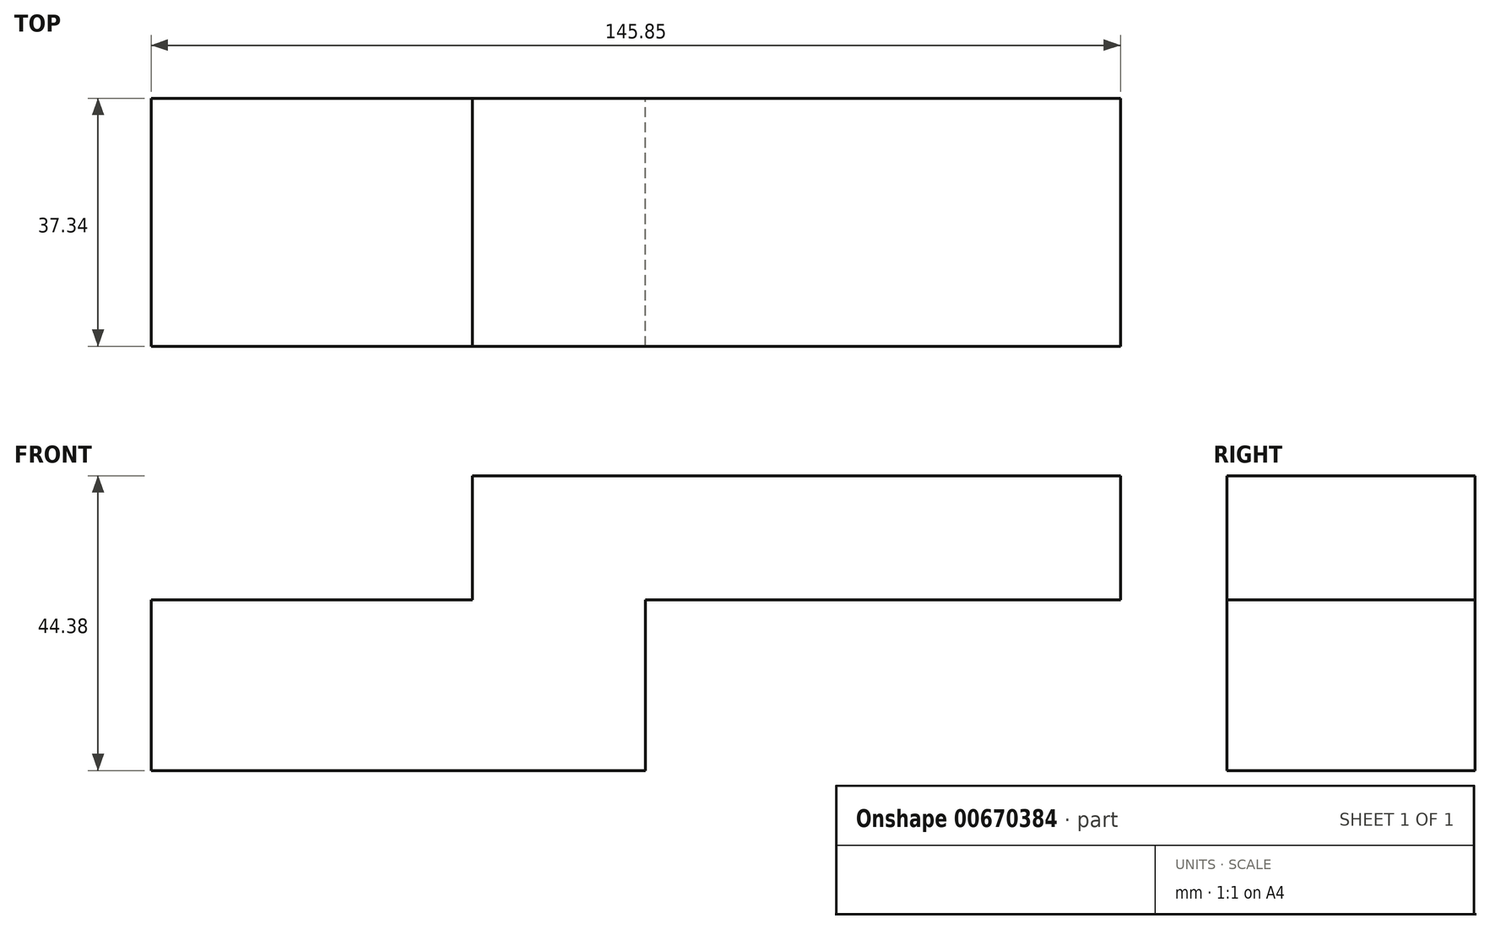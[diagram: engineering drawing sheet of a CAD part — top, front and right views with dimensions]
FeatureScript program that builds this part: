
annotation { "Feature Type Name" : "Feature", "Feature Type Description" : "" }
export const myFeature = defineFeature(function(context is Context, id is Id, definition is map)
    precondition{}
    {
        {
            var Q0;
            Q0=qCreatedBy(makeId("Front.planeOp"),FACE);
            var sketch = newSketch(context, id + "F0", { "sketchPlane" : qUnion([Q0])});
            skLineSegment(sketch, "E0.bottom", {"start": v(0, 0) * mm, "end": v(-74.34, 0) * mm});
            skLineSegment(sketch, "E0.top", {"start": v(0, 25.67) * mm, "end": v(-74.34, 25.67) * mm});
            skLineSegment(sketch, "E0.left", {"start": v(0, 0) * mm, "end": v(0, 25.67) * mm});
            skLineSegment(sketch, "E0.right", {"start": v(-74.34, 0) * mm, "end": v(-74.34, 25.67) * mm});
            skLineSegment(sketch, "E1.bottom", {"start": v(-26.01, 25.67) * mm, "end": v(71.51, 25.67) * mm});
            skLineSegment(sketch, "E1.top", {"start": v(-26.01, 44.38) * mm, "end": v(71.51, 44.38) * mm});
            skLineSegment(sketch, "E1.left", {"start": v(-26.01, 25.67) * mm, "end": v(-26.01, 44.38) * mm});
            skLineSegment(sketch, "E1.right", {"start": v(71.51, 25.67) * mm, "end": v(71.51, 44.38) * mm});
            skLineSegment(sketch, "E2.bottom", {"start": v(71.51, 44.38) * mm, "end": v(36.14, 44.38) * mm});
            skLineSegment(sketch, "E2.top", {"start": v(71.51, 64.3) * mm, "end": v(36.14, 64.3) * mm});
            skLineSegment(sketch, "E2.left", {"start": v(71.51, 44.38) * mm, "end": v(71.51, 64.3) * mm});
            skLineSegment(sketch, "E2.right", {"start": v(36.14, 44.38) * mm, "end": v(36.14, 64.3) * mm});
            skArc(sketch, "E3", {"start": v(62.88, 89.4) * mm, "mid": v(48.73, 80.32) * mm, "end": v(53.83, 64.3) * mm});
            skArc(sketch, "E4", {"start": v(89.32, 80.48) * mm, "mid": v(76.33, 85.64) * mm, "end": v(62.88, 89.4) * mm});
            skSolve(sketch);
        }
        {
            var Q0;
            Q0=makeQuery(id+"F0.imprint","IMPRINT",FACE,{"disambiguationData":[TD([[makeQuery(id+"F0.imprint","IMPRINT",EDGE,{"derivedFrom":sQuery(id+"F0.wireOp",EDGE,"E2.bottom")}),-1.0]])]});
            var Q1;
            Q1=makeQuery(id+"F0.imprint","IMPRINT",FACE,{"disambiguationData":[TD([[makeQuery(id+"F0.imprint","IMPRINT",EDGE,{"derivedFrom":sQuery(id+"F0.wireOp",EDGE,"E0.bottom")}),-1.0]])]});
            var Q2;
            Q2=makeQuery(id+"F0.imprint","IMPRINT",FACE,{"disambiguationData":[TD([[makeQuery(id+"F0.imprint","IMPRINT",EDGE,{"derivedFrom":sQuery(id+"F0.wireOp",EDGE,"E1.top")}),-1.0]])]});
            extrude(context, id + "F1", {"entities" : qUnion([Q0, Q1, Q2]), "depth" : 37.34 * mm, "offsetDistance" : 25.4 * mm});
        }
    });
